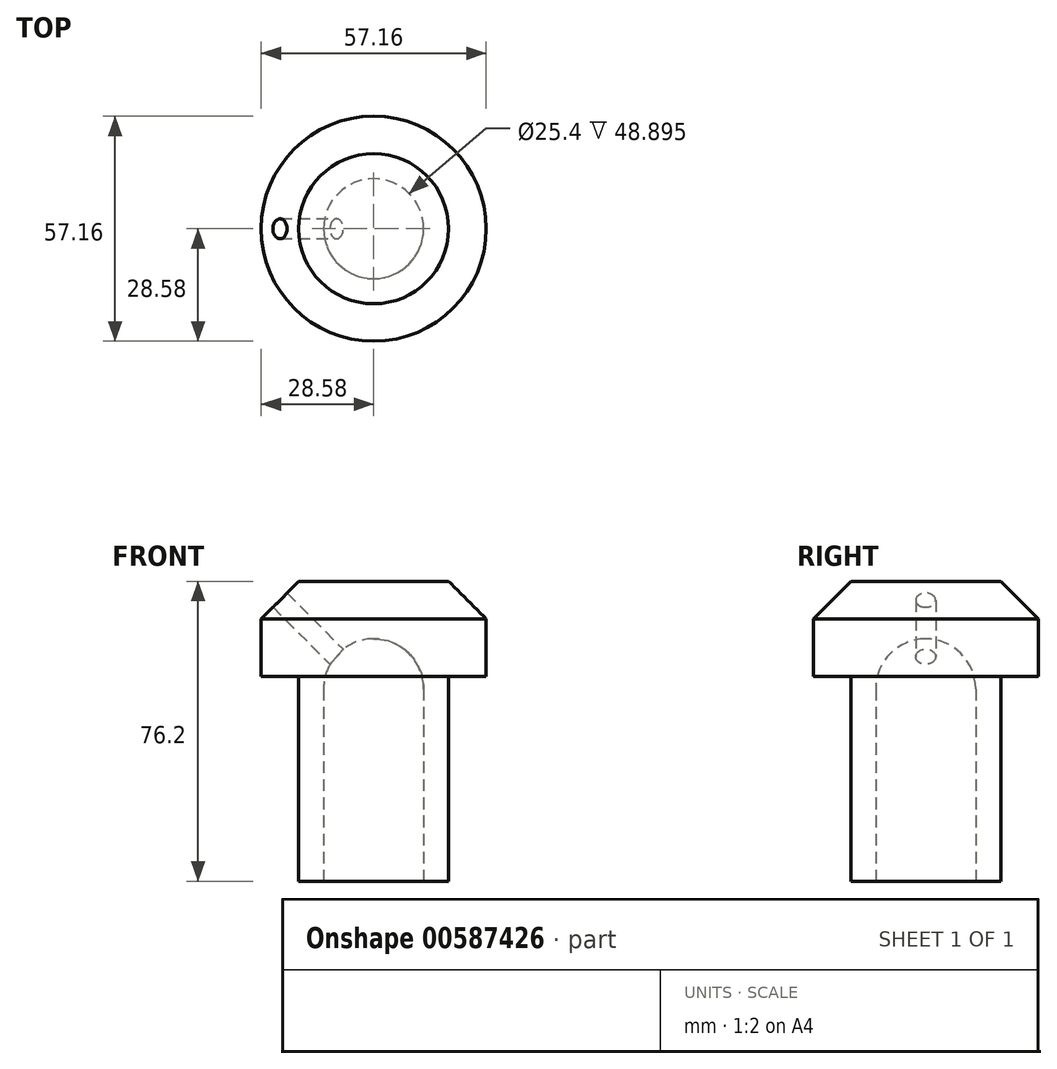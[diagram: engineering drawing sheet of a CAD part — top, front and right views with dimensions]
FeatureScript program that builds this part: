
annotation { "Feature Type Name" : "Feature", "Feature Type Description" : "" }
export const myFeature = defineFeature(function(context is Context, id is Id, definition is map)
    precondition{}
    {
        {
            var Q0;
            Q0=qCreatedBy(makeId("Front.planeOp"),FACE);
            var sketch = newSketch(context, id + "F0", { "sketchPlane" : qUnion([Q0])});
            skLineSegment(sketch, "E0", {"start": v(0, 43.58) * mm, "end": v(0, -47) * mm, "construction": true});
            skLineSegment(sketch, "E1", {"start": v(0, 0) * mm, "end": v(-19.05, 0) * mm});
            skLineSegment(sketch, "E2", {"start": v(-19.05, 0) * mm, "end": v(-28.58, -9.53) * mm});
            skLineSegment(sketch, "E3", {"start": v(-28.58, -9.53) * mm, "end": v(-28.58, -24.13) * mm});
            skLineSegment(sketch, "E4", {"start": v(-28.58, -24.13) * mm, "end": v(-19.05, -24.13) * mm});
            skLineSegment(sketch, "E5", {"start": v(-19.05, -24.13) * mm, "end": v(-19.05, -76.2) * mm});
            skLineSegment(sketch, "E6", {"start": v(-19.05, -76.2) * mm, "end": v(0, -76.2) * mm});
            skLineSegment(sketch, "E7", {"start": v(0, -76.2) * mm, "end": v(0, 0) * mm});
            skSolve(sketch);
        }
        {
            var Q0;
            Q0=makeQuery(id+"F0.imprint","IMPRINT",FACE,{"disambiguationData":[TD([[makeQuery(id+"F0.imprint","IMPRINT",EDGE,{"derivedFrom":sQuery(id+"F0.wireOp",EDGE,"E1")}),1.0]])]});
            var Q1;
            Q1=sQuery(id+"F0.wireOp",EDGE,"E0");
            revolve(context, id + "F1", {"entities" : qUnion([Q0]), "axis" : qUnion([Q1]), "revolveType" : RevolveType.FULL});
        }
        {
            var Q0;
            Q0=qCreatedBy(makeId("Front.planeOp"),FACE);
            var sketch = newSketch(context, id + "F2", { "sketchPlane" : qUnion([Q0])});
            skLineSegment(sketch, "E8", {"start": v(0, -95.55) * mm, "end": v(0, 8.78) * mm, "construction": true});
            skPoint(sketch, "E9", {"position": v(0, -27.3) * mm});
            skArc(sketch, "E10", {"start": v(-12.7, -27.3) * mm, "mid": v(-8.98, -18.32) * mm, "end": v(0, -14.6) * mm});
            skLineSegment(sketch, "E11", {"start": v(-12.7, -27.3) * mm, "end": v(-12.7, -76.2) * mm});
            skPoint(sketch, "E12.orphan", {"position": v(12.7, -27.3) * mm});
            skLineSegment(sketch, "E13", {"start": v(0, -14.6) * mm, "end": v(0, -76.2) * mm});
            skLineSegment(sketch, "E14", {"start": v(0, -76.2) * mm, "end": v(-12.7, -76.2) * mm});
            skSolve(sketch);
        }
        {
            var Q0;
            Q0 = qSketchRegion(id + "F2", true);
            var Q1;
            Q1=sQuery(id+"F2.wireOp",EDGE,"E13");
            revolve(context, id + "F3", {"operationType" : NewBodyOperationType.REMOVE, "entities" : qUnion([Q0]), "axis" : qUnion([Q1]), "revolveType" : RevolveType.FULL, "oppositeDirection" : true});
        }
        {
            var Q0;
            Q0=qCreatedBy(makeId("Front.planeOp"),FACE);
            var sketch = newSketch(context, id + "F4", { "sketchPlane" : qUnion([Q0])});
            skPoint(sketch, "E15", {"position": v(-28.58, -9.53) * mm});
            skPoint(sketch, "E16", {"position": v(-19.05, 0) * mm});
            skPoint(sketch, "E17", {"position": v(-23.81, -4.76) * mm});
            skLineSegment(sketch, "E18", {"start": v(-23.81, -4.76) * mm, "end": v(-5.85, -22.72) * mm, "construction": true});
            skLineSegment(sketch, "E19", {"start": v(-25.6, -6.56) * mm, "end": v(-7.65, -24.52) * mm});
            skLineSegment(sketch, "E20", {"start": v(-25.6, -6.56) * mm, "end": v(-23.81, -4.76) * mm});
            skLineSegment(sketch, "E21", {"start": v(-5.85, -22.72) * mm, "end": v(-7.65, -24.52) * mm});
            skLineSegment(sketch, "E22", {"start": v(-23.81, -4.76) * mm, "end": v(-5.85, -22.72) * mm});
            skSolve(sketch);
        }
        {
            var Q0;
            Q0 = qSketchRegion(id + "F4", true);
            var Q1;
            Q1=sQuery(id+"F4.wireOp",EDGE,"E22");
            revolve(context, id + "F5", {"operationType" : NewBodyOperationType.REMOVE, "entities" : qUnion([Q0]), "axis" : qUnion([Q1]), "revolveType" : RevolveType.FULL, "oppositeDirection" : true});
        }
    });
